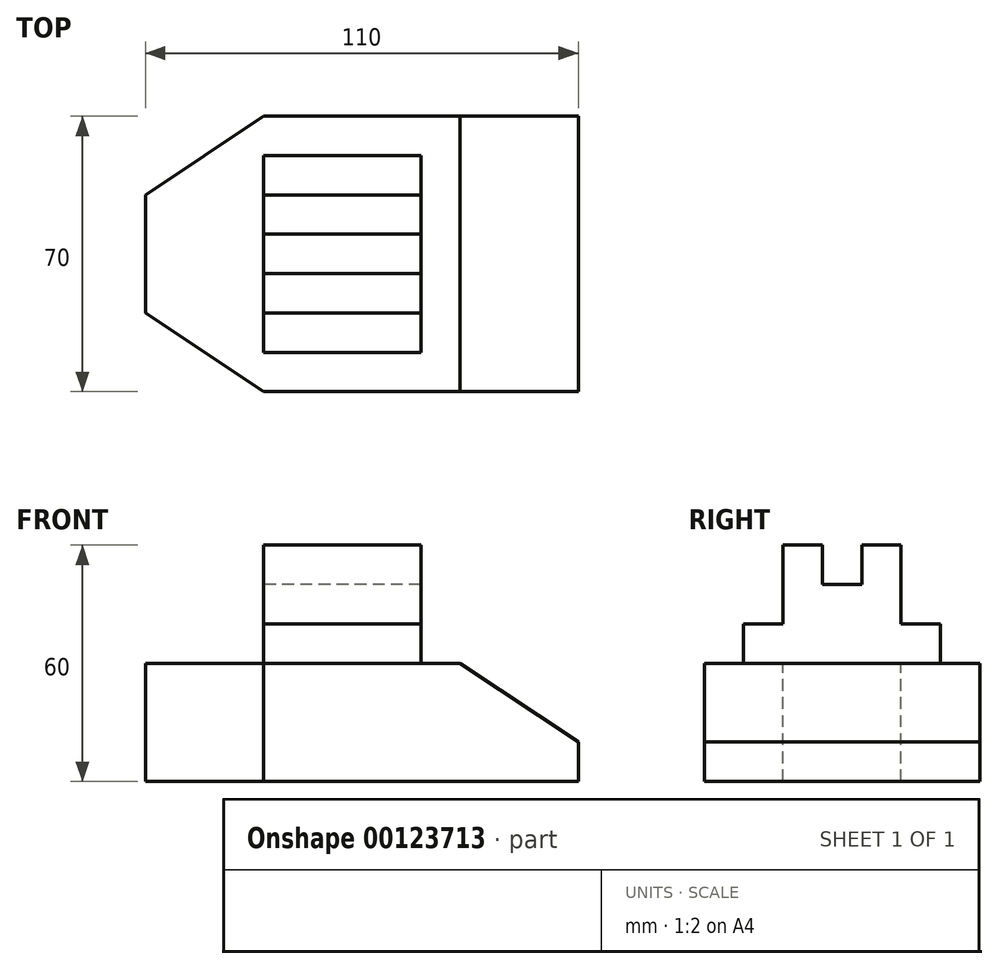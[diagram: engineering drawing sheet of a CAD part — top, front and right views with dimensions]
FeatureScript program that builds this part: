
annotation { "Feature Type Name" : "Feature", "Feature Type Description" : "" }
export const myFeature = defineFeature(function(context is Context, id is Id, definition is map)
    precondition{}
    {
        {
            var Q0;
            Q0=qCreatedBy(makeId("Front.planeOp"),FACE);
            var sketch = newSketch(context, id + "F0", { "sketchPlane" : qUnion([Q0])});
            skLineSegment(sketch, "E0", {"start": v(0, 0) * mm, "end": v(110, 0) * mm});
            skLineSegment(sketch, "E1", {"start": v(110, 0) * mm, "end": v(110, 10) * mm});
            skLineSegment(sketch, "E2", {"start": v(110, 10) * mm, "end": v(80, 30) * mm});
            skLineSegment(sketch, "E3", {"start": v(80, 30) * mm, "end": v(0, 30) * mm});
            skLineSegment(sketch, "E4", {"start": v(0, 30) * mm, "end": v(0, 0) * mm});
            skLineSegment(sketch, "E5", {"start": v(70, 30) * mm, "end": v(70, 60) * mm});
            skLineSegment(sketch, "E6", {"start": v(70, 60) * mm, "end": v(30, 60) * mm});
            skLineSegment(sketch, "E7", {"start": v(30, 60) * mm, "end": v(30, 30) * mm});
            skSolve(sketch);
        }
        {
            var Q0;
            Q0=makeQuery(id+"F0.imprint","IMPRINT",FACE,{"disambiguationData":[TD([[makeQuery(id+"F0.imprint","IMPRINT",EDGE,{"derivedFrom":sQuery(id+"F0.wireOp",EDGE,"E0")}),1.0]])]});
            extrude(context, id + "F1", {"entities" : qUnion([Q0]), "endBound" : BoundingType.SYMMETRIC, "depth" : 70 * mm});
        }
        {
            var Q0;
            {var subQ0=sQuery(id+"F0.wireOp",EDGE,"E5");Q0=makeQuery(id+"F0.imprint","IMPRINT",FACE,{"disambiguationData":[TD([[makeQuery(id+"F0.imprint","IMPRINT",EDGE,{"derivedFrom":subQ0}),1.0]])]});}
            extrude(context, id + "F2", {"entities" : qUnion([Q0]), "operationType" : NewBodyOperationType.ADD, "endBound" : BoundingType.SYMMETRIC, "depth" : 50 * mm});
        }
        {
            var Q0;
            Q0=makeQuery(id+"F1.opExtrude","SWEPT_FACE",FACE,{"disambiguationData":[OSD([sQuery(id+"F0.wireOp",EDGE,"E3")])]});
            var sketch = newSketch(context, id + "F3", { "sketchPlane" : qUnion([Q0])});
            skLineSegment(sketch, "E8", {"start": v(30, 35) * mm, "end": v(0, 15) * mm});
            skLineSegment(sketch, "E9", {"start": v(0, 15) * mm, "end": v(0, 35) * mm});
            skLineSegment(sketch, "E10", {"start": v(0, 35) * mm, "end": v(30, 35) * mm});
            skLineSegment(sketch, "E11", {"start": v(30, -35) * mm, "end": v(0, -15) * mm});
            skLineSegment(sketch, "E12", {"start": v(0, -15) * mm, "end": v(0, -35) * mm});
            skLineSegment(sketch, "E13", {"start": v(0, -35) * mm, "end": v(30, -35) * mm});
            skSolve(sketch);
        }
        {
            var Q0;
            Q0=makeQuery(id+"F3.imprint","IMPRINT",FACE,{"disambiguationData":[TD([[makeQuery(id+"F3.imprint","IMPRINT",EDGE,{"derivedFrom":sQuery(id+"F3.wireOp",EDGE,"E11")}),1.0]])]});
            var Q1;
            Q1=makeQuery(id+"F3.imprint","IMPRINT",FACE,{"disambiguationData":[TD([[makeQuery(id+"F3.imprint","IMPRINT",EDGE,{"derivedFrom":sQuery(id+"F3.wireOp",EDGE,"E8")}),-1.0]])]});
            extrude(context, id + "F4", {"entities" : qUnion([Q0, Q1]), "operationType" : NewBodyOperationType.REMOVE, "endBound" : BoundingType.THROUGH_ALL, "oppositeDirection" : true, "depth" : 25 * mm});
        }
        {
            var Q0;
            Q0=makeQuery(id+"F2.opExtrude","SWEPT_FACE",FACE,{"disambiguationData":[OSD([sQuery(id+"F0.wireOp",EDGE,"E7")])]});
            var sketch = newSketch(context, id + "F5", { "sketchPlane" : qUnion([Q0])});
            skLineSegment(sketch, "E14", {"start": v(-25, 60) * mm, "end": v(-25, 40) * mm});
            skLineSegment(sketch, "E15", {"start": v(-25, 40) * mm, "end": v(-15, 40) * mm});
            skLineSegment(sketch, "E16", {"start": v(-15, 40) * mm, "end": v(-15, 60) * mm});
            skLineSegment(sketch, "E17", {"start": v(-15, 60) * mm, "end": v(-25, 60) * mm});
            skLineSegment(sketch, "E18", {"start": v(25, 60) * mm, "end": v(15, 60) * mm});
            skLineSegment(sketch, "E19", {"start": v(15, 60) * mm, "end": v(15, 40) * mm});
            skLineSegment(sketch, "E20", {"start": v(15, 40) * mm, "end": v(25, 40) * mm});
            skLineSegment(sketch, "E21", {"start": v(25, 40) * mm, "end": v(25, 60) * mm});
            skSolve(sketch);
        }
        {
            var Q0;
            Q0 = qSketchRegion(id + "F5", true);
            extrude(context, id + "F6", {"entities" : qUnion([Q0]), "operationType" : NewBodyOperationType.REMOVE, "endBound" : BoundingType.THROUGH_ALL, "oppositeDirection" : true, "depth" : 25 * mm});
        }
        {
            var Q0;
            Q0=makeQuery(id+"F2.opExtrude","SWEPT_FACE",FACE,{"disambiguationData":[OSD([sQuery(id+"F0.wireOp",EDGE,"E7")])]});
            var sketch = newSketch(context, id + "F7", { "sketchPlane" : qUnion([Q0])});
            skPoint(sketch, "E22.endSnap0", {"position": v(0, 60) * mm});
            skLineSegment(sketch, "E23.0", {"start": v(-5, 60) * mm, "end": v(-5, 50) * mm});
            skLineSegment(sketch, "E24.0", {"start": v(5, 60) * mm, "end": v(5, 50) * mm});
            skLineSegment(sketch, "E25", {"start": v(-5, 50) * mm, "end": v(5, 50) * mm});
            skLineSegment(sketch, "E26", {"start": v(5, 60) * mm, "end": v(-5, 60) * mm});
            skSolve(sketch);
        }
        {
            var Q0;
            Q0 = qSketchRegion(id + "F7", true);
            extrude(context, id + "F8", {"entities" : qUnion([Q0]), "operationType" : NewBodyOperationType.REMOVE, "endBound" : BoundingType.THROUGH_ALL, "oppositeDirection" : true, "depth" : 25 * mm});
        }
    });
